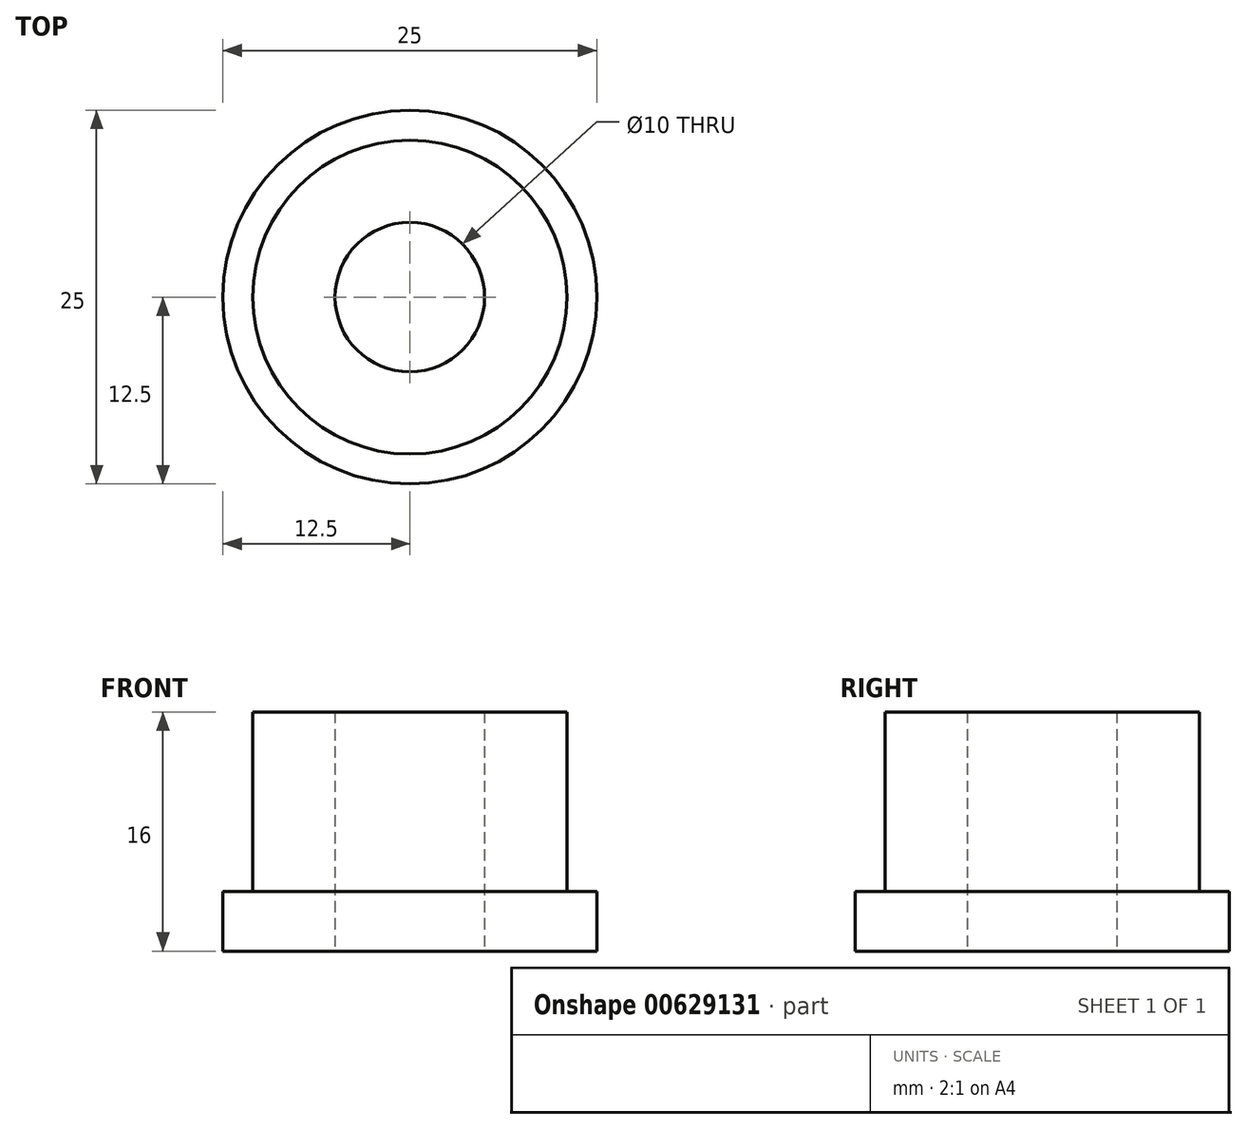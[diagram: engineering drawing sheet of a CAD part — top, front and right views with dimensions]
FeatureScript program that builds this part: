
annotation { "Feature Type Name" : "Feature", "Feature Type Description" : "" }
export const myFeature = defineFeature(function(context is Context, id is Id, definition is map)
    precondition{}
    {
        {
            var Q0;
            Q0=qCreatedBy(makeId("Top.planeOp"),FACE);
            var sketch = newSketch(context, id + "F0", { "sketchPlane" : qUnion([Q0])});
            skCircle(sketch, "E0", {"center": v(0, 0) * mm, "radius": 12.5 * mm});
            skCircle(sketch, "E1", {"center": v(0, 0) * mm, "radius": 5 * mm});
            skSolve(sketch);
        }
        {
            var Q0;
            Q0=makeQuery(id+"F0.imprint","IMPRINT",FACE,{"disambiguationData":[TD([[makeQuery(id+"F0.imprint","IMPRINT",EDGE,{"derivedFrom":sQuery(id+"F0.wireOp",EDGE,"E0")}),1.0]])]});
            extrude(context, id + "F1", {"entities" : qUnion([Q0]), "depth" : 4 * mm, "offsetDistance" : 25 * mm});
        }
        {
            var Q0;
            Q0=makeQuery(id+"F1.opExtrude","CAP_FACE",FACE,{"disambiguationData":[OSD([sQuery(id+"F0.wireOp",EDGE,"E0"),sQuery(id+"F0.wireOp",EDGE,"E1")])],"isStart":false});
            var sketch = newSketch(context, id + "F2", { "sketchPlane" : qUnion([Q0])});
            skCircle(sketch, "E2", {"center": v(0, 0) * mm, "radius": 10.5 * mm});
            skCircle(sketch, "E3", {"center": v(0, 0) * mm, "radius": 5 * mm});
            skSolve(sketch);
        }
        {
            var Q0;
            Q0 = qSketchRegion(id + "F2", true);
            extrude(context, id + "F3", {"entities" : qUnion([Q0]), "operationType" : NewBodyOperationType.ADD, "depth" : 12 * mm, "offsetDistance" : 25 * mm});
        }
    });
